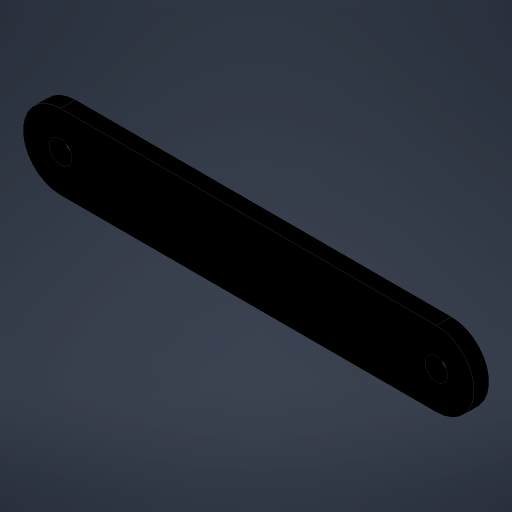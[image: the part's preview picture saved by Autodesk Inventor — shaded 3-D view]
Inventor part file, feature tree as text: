
AUTODESK INVENTOR PART (.ipt)
format: ipt  version: 2023 (Build 270158000, 158)  size: 185,344 bytes
history: native  units: mm
features: extrude x2, sketch x2, fillet x1
ambient origin geometry x8: Origin, YZ Plane, XZ Plane, XY Plane, X Axis, Y Axis, Z Axis, Center Point
bodies: Solid1 (feature_tree)
feature tree (5):
  extrude  "Extrusion1"  Depth=10.0mm
  fillet  "Fillet1"  Radius=2.0mm
  extrude  "Extrusion2"  Depth=2.0mm
  sketch  "Sketch1"  dims[d0=60.0mm d1=10.0mm d2=2.0mm d3=0.0mm]
  sketch  "Sketch2"  dims[d4=5.0mm d5=3.0mm d6=3.0mm d7=2.0mm d8=0.0mm]
